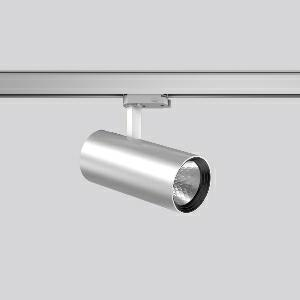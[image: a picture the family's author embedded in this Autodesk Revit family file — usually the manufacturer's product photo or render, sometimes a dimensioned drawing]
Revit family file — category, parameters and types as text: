
# Revit family: deecos_s_mini_742203_004_2_94a4
name_source: partatom
category: Lighting Fixtures
units: mm (PartAtom-declared; Revit-internal decimal feet)

## family parameters
Cut with Voids When Loaded = No
Host = Face
Light Source = No
Part Type = Normal
Room Calculation Point = No
Round Connector Dimension = Use Diameter
Shared = No

## types (1)
- DEECOS S mini (1 x LED Modul 927, 3400 lm, 2700)
    Apparent Load = 29 VA
    Approval mark = CE
    CIE Flux Codes = 100 100 100 100 100
    Color Rendering = 92
    Color Temperature = 2700
    Default Elevation = 1800 mm
    Description = Series: DEECOS S mini
LED surface-mounted projector in modern design with no visible cooling ribs. Housing: die-cast aluminium, powder-coated. Rotation range: 356°. Swivel range: 90°. Black plastic ring and recessed LED to prevent glare from the side. Optical assembly with reflector made of MIRO-Silver with 98% total light reflection for outstanding efficiency - can be changed without tools. Best colour rendering index Ra>90. With multi adaptor for 3-circuit tracks 230 V. Suitable for Track on ceiling, Wall track. High quality converter without flickering and stroboscopic effect. The following accessories can be mounted without use of tools: interchangeable lenses, decorative glasses, honeycomb louvre, clear and frosted diffusers, white interchangeable plastic ring. 
Colour: silver
Diameter: 87 mm
Height: 214 mm
Lamp: LED
Socket: without socket
Colour temperature: 2700K
Colour rendering index (CRI): 92
System power: 29 W
Rated luminous flux: 3400 lm
Luminous efficiency: 117 lm/W
Control gear: Regulated power supply
Protection class: I
Type of protection: IP 20
    Height = 214 mm
    Lamp = 1 x LED Modul 927
    Lamp Light Flux = 3400 lm
    Lamp count = 1
    Length = 87 mm
    Lifetime = 50000 h
    Luminous efficacy = 117 lm/W
    Manufacturer = RZB
    ModVariant = No
    Model = 742203.004.2
    Mounting Place = Ceiling
    Mounting Type = Rail mounted
    Number of Poles = 1
    OnlyDefault = Yes
    Power Factor = 1
    Product Name = DEECOS S mini
    Product group = Track mounted projectors
    ProductGroupID = 301
    Protection Class = Protection class I
    Protection Degree = IP 20
    RLX_Detail_Level = 1
    RLX_Emergency_Light_Flux = 0 lm
    RLX_Emergency_Type = 0
    RLX_Emergency_Type_DB = No
    RlxData = <blob elided: 36845 chars, md5=4e73eeae>
    Socket = socket
    Standby Power = 0 W
    System Light Flux = 3400 lm
    System Power = 29 W
    Type Comments = Product without accessories
    Type Image = 741926.004.jpg
    URL = http://relux.com
    VarID = ---
    Voltage = 230 V
    Voltage Range = 220-240 V
    Weight = 0.00 kg
    Width = 0 mm  [stored 0 ft]

note: [stored X ft] marks values corroborated as IEEE doubles in the binary element streams (Revit-internal decimal feet)

## geometry (parser evidence)
native form markers: Blend x4, Sweep x11
no freeform markers — native parametric forms only
